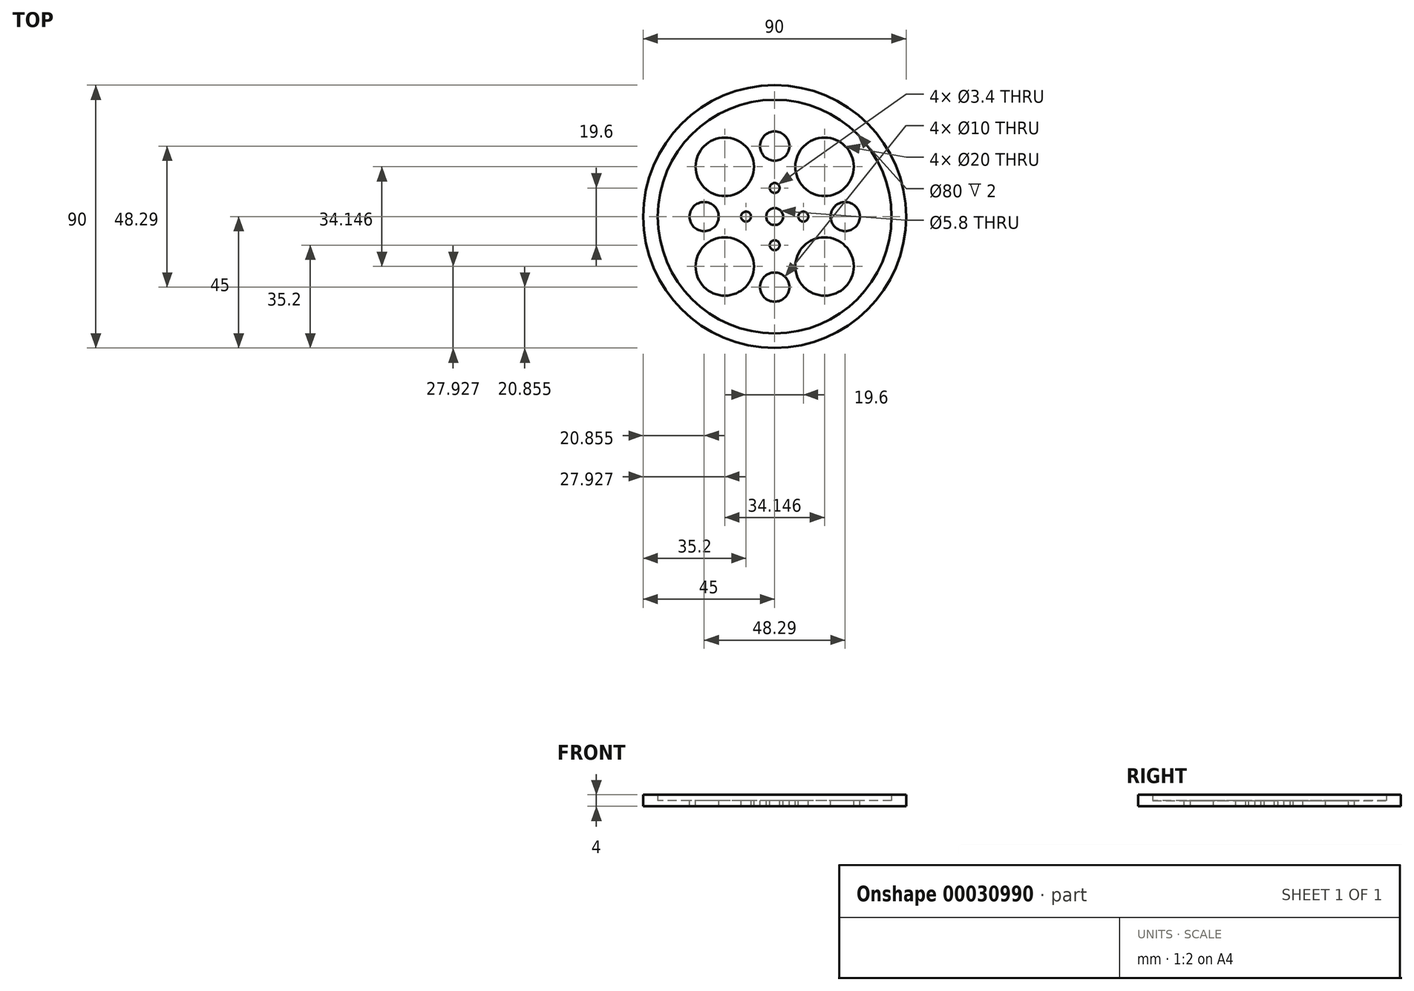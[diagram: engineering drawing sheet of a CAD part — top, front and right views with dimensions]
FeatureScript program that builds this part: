
annotation { "Feature Type Name" : "Feature", "Feature Type Description" : "" }
export const myFeature = defineFeature(function(context is Context, id is Id, definition is map)
    precondition{}
    {
        {
            var Q0;
            Q0=qCreatedBy(makeId("Top.planeOp"),FACE);
            var sketch = newSketch(context, id + "F0", { "sketchPlane" : qUnion([Q0])});
            skCircle(sketch, "E0", {"center": v(0, 0) * mm, "radius": 40 * mm});
            skCircle(sketch, "E1.0", {"center": v(0, 0) * mm, "radius": 45 * mm});
            skCircle(sketch, "E2.cCircle", {"center": v(0, 0) * mm, "radius": 22.3 * mm, "construction": true});
            skLineSegment(sketch, "E2.0", {"start": v(0, 24.15) * mm, "end": v(17.07, 17.07) * mm, "construction": true});
            skLineSegment(sketch, "E2.1", {"start": v(17.07, 17.07) * mm, "end": v(24.15, 0) * mm, "construction": true});
            skLineSegment(sketch, "E2.2", {"start": v(24.15, 0) * mm, "end": v(17.07, -17.07) * mm, "construction": true});
            skLineSegment(sketch, "E2.3", {"start": v(17.07, -17.07) * mm, "end": v(0, -24.15) * mm, "construction": true});
            skLineSegment(sketch, "E2.4", {"start": v(0, -24.15) * mm, "end": v(-17.07, -17.07) * mm, "construction": true});
            skLineSegment(sketch, "E2.5", {"start": v(-17.07, -17.07) * mm, "end": v(-24.15, 0) * mm, "construction": true});
            skLineSegment(sketch, "E2.6", {"start": v(-24.15, 0) * mm, "end": v(-17.07, 17.07) * mm, "construction": true});
            skLineSegment(sketch, "E2.7", {"start": v(-17.07, 17.07) * mm, "end": v(0, 24.15) * mm, "construction": true});
            skPoint(sketch, "E2.0.midPoint", {"position": v(8.54, 20.6) * mm});
            skCircle(sketch, "E3", {"center": v(-17.07, 17.07) * mm, "radius": 10 * mm});
            skCircle(sketch, "E4", {"center": v(0, 24.15) * mm, "radius": 5 * mm});
            skCircle(sketch, "E5", {"center": v(17.07, 17.07) * mm, "radius": 10 * mm});
            skCircle(sketch, "E6", {"center": v(24.15, 0) * mm, "radius": 5 * mm});
            skCircle(sketch, "E7", {"center": v(17.07, -17.07) * mm, "radius": 10 * mm});
            skCircle(sketch, "E8", {"center": v(0, -24.15) * mm, "radius": 5 * mm});
            skCircle(sketch, "E9", {"center": v(-17.07, -17.07) * mm, "radius": 10 * mm});
            skCircle(sketch, "E10", {"center": v(-24.15, 0) * mm, "radius": 5 * mm});
            skCircle(sketch, "E11", {"center": v(0, 0) * mm, "radius": 2.9 * mm});
            skCircle(sketch, "E12.0", {"center": v(0, 0) * mm, "radius": 4.4 * mm});
            skCircle(sketch, "E13", {"center": v(0, 9.8) * mm, "radius": 1.7 * mm});
            skCircle(sketch, "E14.1.0", {"center": v(-9.8, 0) * mm, "radius": 1.7 * mm});
            skCircle(sketch, "E14.2.0", {"center": v(0, -9.8) * mm, "radius": 1.7 * mm});
            skCircle(sketch, "E14.3.0", {"center": v(9.8, 0) * mm, "radius": 1.7 * mm});
            skLineSegment(sketch, "E15", {"start": v(0, 24.15) * mm, "end": v(0, 0) * mm, "construction": true});
            skSolve(sketch);
        }
        {
            var Q0;
            Q0 = qSketchRegion(id + "F0", true);
            extrude(context, id + "F1", {"entities" : qUnion([Q0]), "endBound" : BoundingType.SYMMETRIC, "depth" : 4 * mm});
        }
        {
            var Q0;
            Q0=makeQuery(id+"F0.imprint","IMPRINT",FACE,{"disambiguationData":[TD([[makeQuery(id+"F0.imprint","IMPRINT",EDGE,{"derivedFrom":sQuery(id+"F0.wireOp",EDGE,"E0")}),1.0]])]});
            var Q1;
            Q1=makeQuery(id+"F0.imprint","IMPRINT",FACE,{"disambiguationData":[TD([[makeQuery(id+"F0.imprint","IMPRINT",EDGE,{"derivedFrom":sQuery(id+"F0.wireOp",EDGE,"E11")}),-1.0]])]});
            var Q2;
            Q2=makeQuery(id+"F1.opExtrude","CAP_FACE",FACE,{"disambiguationData":[OSD([sQuery(id+"F0.wireOp",EDGE,"E0"),sQuery(id+"F0.wireOp",EDGE,"E1.0")])],"isStart":true});
            extrude(context, id + "F2", {"entities" : qUnion([Q0, Q1]), "operationType" : NewBodyOperationType.ADD, "endBound" : BoundingType.UP_TO_SURFACE, "oppositeDirection" : true, "endBoundEntityFace" : qUnion([Q2]), "depth" : 25 * mm});
        }
    });
